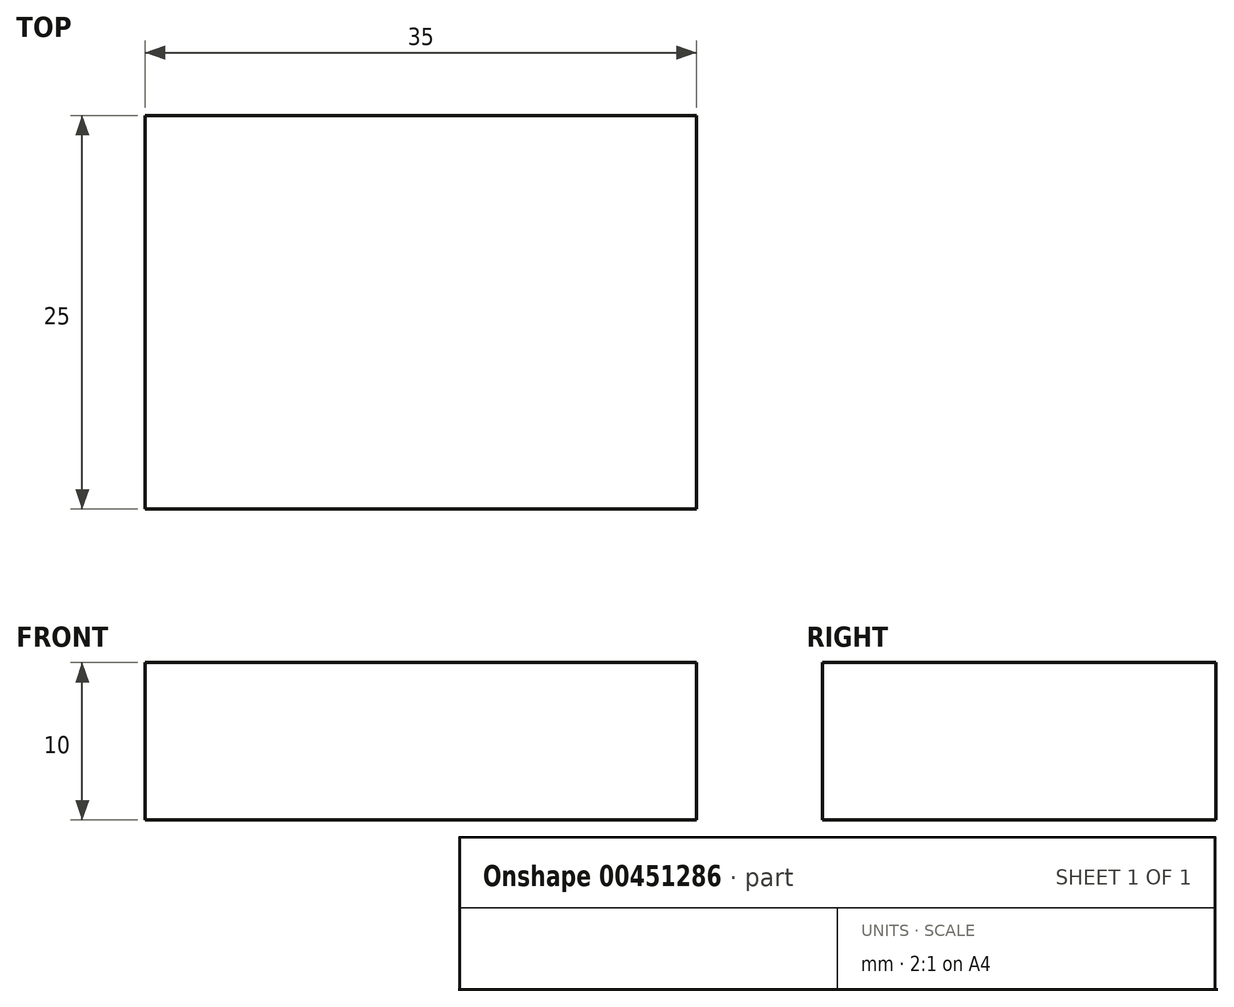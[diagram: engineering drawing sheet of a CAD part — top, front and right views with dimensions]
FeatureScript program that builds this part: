
annotation { "Feature Type Name" : "Feature", "Feature Type Description" : "" }
export const myFeature = defineFeature(function(context is Context, id is Id, definition is map)
    precondition{}
    {
        {
            var Q0;
            Q0=qCreatedBy(makeId("Front.planeOp"),FACE);
            var sketch = newSketch(context, id + "F0", { "sketchPlane" : qUnion([Q0])});
            skLineSegment(sketch, "E0.bottom", {"start": v(0, 0) * mm, "end": v(35, 0) * mm});
            skLineSegment(sketch, "E0.top", {"start": v(0, 10) * mm, "end": v(35, 10) * mm});
            skLineSegment(sketch, "E0.left", {"start": v(0, 0) * mm, "end": v(0, 10) * mm});
            skLineSegment(sketch, "E0.right", {"start": v(35, 0) * mm, "end": v(35, 10) * mm});
            skSolve(sketch);
        }
        {
            var Q0;
            Q0=makeQuery(id+"F0.imprint","IMPRINT",FACE,{"disambiguationData":[TD([[makeQuery(id+"F0.imprint","IMPRINT",EDGE,{"derivedFrom":sQuery(id+"F0.wireOp",EDGE,"E0.bottom")}),1.0]])]});
            extrude(context, id + "F1", {"entities" : qUnion([Q0]), "depth" : 25 * mm});
        }
    });
